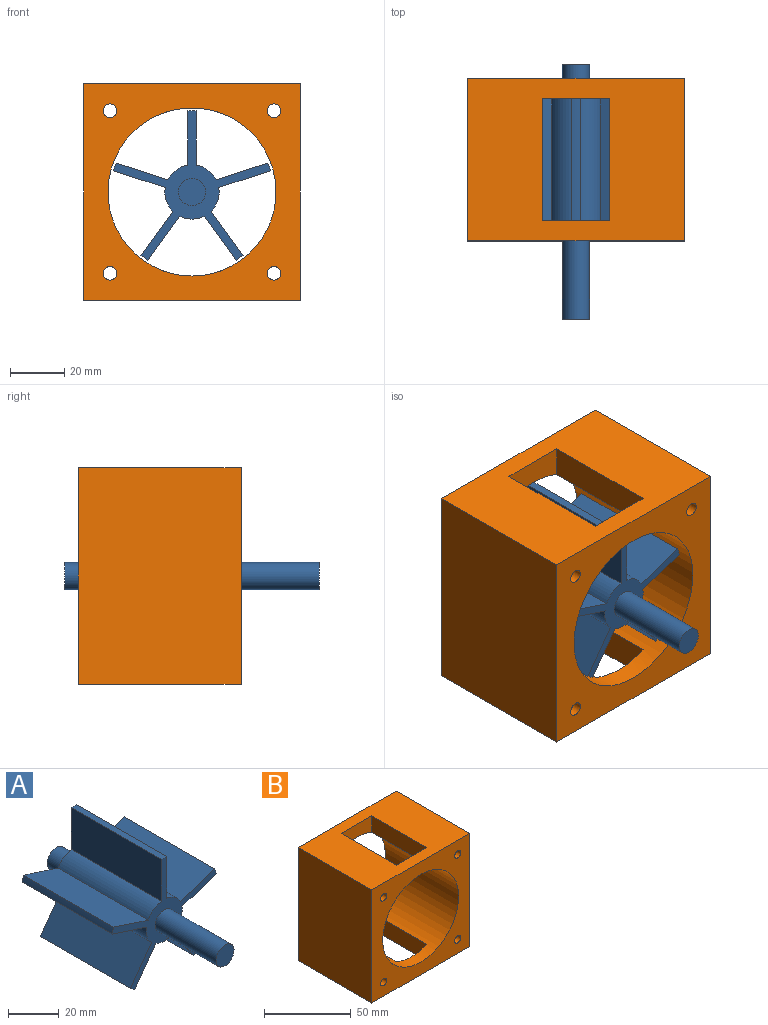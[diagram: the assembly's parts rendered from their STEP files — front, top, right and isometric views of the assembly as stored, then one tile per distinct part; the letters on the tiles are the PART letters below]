
ASSEMBLY  parts=2 mates=1
PART A: 26 faces, bbox 57.9x93.8x55.1 mm
  f0: plane 50x20.08mm, normal (1,0,0), area 1003.8mm2, adj f1,f19,f20,f21
  f1: cylinder r=30mm len=50mm, axis (0,1,0), area 150.1mm2, adj f0,f2,f20,f21
  f2: plane 50x20.08mm, normal (-1,0,0), area 1003.8mm2, adj f1,f3,f20,f21
  f3: cylinder r=10mm len=50mm, axis (0,1,0), area 477.8mm2, adj f2,f4,f20,f21
  f4: plane 50x19.09mm, normal (0.31,0,0.95), area 1003.8mm2, adj f3,f5,f20,f21
  f5: cylinder r=30mm len=50mm, axis (0,1,0), area 150.1mm2, adj f4,f6,f20,f21
  f6: plane 50x19.09mm, normal (-0.31,0,-0.95), area 1003.8mm2, adj f5,f7,f20,f21
  f7: cylinder r=10mm len=50mm, axis (0,1,0), area 477.8mm2, adj f6,f8,f20,f21
  f8: plane 50x16.24mm, normal (-0.81,0,0.59), area 1003.8mm2, adj f7,f9,f20,f21
  f9: cylinder r=30mm len=50mm, axis (0,1,0), area 150.1mm2, adj f8,f10,f20,f21
  f10: plane 50x16.24mm, normal (0.81,0,-0.59), area 1003.8mm2, adj f9,f11,f20,f21
  f11: cylinder r=10mm len=50mm, axis (0,1,0), area 477.8mm2, adj f10,f12,f20,f21
  f12: plane 50x16.24mm, normal (-0.81,0,-0.59), area 1003.8mm2, adj f11,f13,f20,f21
  f13: cylinder r=30mm len=50mm, axis (0,1,0), area 150.1mm2, adj f12,f14,f20,f21
  f14: plane 50x16.24mm, normal (0.81,0,0.59), area 1003.8mm2, adj f13,f15,f20,f21
  f15: cylinder r=10mm len=50mm, axis (0,1,0), area 477.8mm2, adj f14,f16,f20,f21
  f16: plane 50x19.09mm, normal (0.31,0,-0.95), area 1003.8mm2, adj f15,f17,f20,f21
  f17: cylinder r=30mm len=50mm, axis (0,1,0), area 150.1mm2, adj f16,f18,f20,f21
  f18: plane 50x19.09mm, normal (-0.31,0,0.95), area 1003.8mm2, adj f17,f19,f20,f21
  f19: cylinder r=10mm len=50mm, axis (0,1,0), area 477.8mm2, adj f0,f18,f20,f21
  f20: plane 57.92x55.12mm, normal (0,-1,0), area 536mm2, adj f0,f1,f2,f3,f4,f5,f6,f7
  f21: plane 57.92x55.12mm, normal (0,1,0), area 536mm2, adj f0,f1,f2,f3,f4,f5,f6,f7
  f22: cylinder r=5mm len=33.8mm, axis (0,1,0), area 1061.9mm2, adj f20,f23
  f23: plane 10x10mm, normal (0,-1,0), area 78.5mm2, adj f22
  f24: cylinder r=5mm len=10mm, axis (0,-1,0), area 314.2mm2, adj f21,f25
  f25: plane 10x10mm, normal (0,1,0), area 78.5mm2, adj f24
PART B: 19 faces, bbox 80x60x80 mm
  f0: plane 80x80mm, normal (0,-1,0), area 3302.4mm2, adj f2,f3,f4,f5,f6,f15,f16,f17
  f1: plane 80x80mm, normal (0,1,0), area 3302.4mm2, adj f2,f3,f4,f5,f6,f15,f16,f17
  f2: plane 80x60mm, normal (0,0,1), area 3675mm2, adj f0,f1,f5,f6,f11,f12,f13,f14
  f3: plane 80x60mm, normal (0,0,-1), area 3675mm2, adj f0,f1,f5,f6,f7,f8,f9,f10
  f4: cylinder r=31mm len=62mm, axis (0,1,0), area 9370.8mm2, adj f0,f1,f7,f8,f9,f10,f11,f12
  f5: plane 80x60mm, normal (-1,0,0), area 4800mm2, adj f0,f1,f2,f3
  f6: plane 80x60mm, normal (1,0,0), area 4800mm2, adj f0,f1,f2,f3
  f7: plane 45x11.63mm, normal (-1,0,0), area 523.4mm2, adj f3,f4,f8,f10
  f8: plane 25x11.63mm, normal (0,1,0), area 246.5mm2, adj f3,f4,f7,f9
  f9: plane 45x11.63mm, normal (1,0,0), area 523.4mm2, adj f3,f4,f8,f10
  f10: plane 25x11.63mm, normal (0,-1,0), area 246.5mm2, adj f3,f4,f7,f9
  f11: plane 25x11.63mm, normal (0,-1,0), area 246.5mm2, adj f2,f4,f12,f14
  f12: plane 45x11.63mm, normal (1,0,0), area 523.4mm2, adj f2,f4,f11,f13
  f13: plane 25x11.63mm, normal (0,1,0), area 246.5mm2, adj f2,f4,f12,f14
  f14: plane 45x11.63mm, normal (-1,0,0), area 523.4mm2, adj f2,f4,f11,f13
  f15: cylinder r=2.5mm len=60mm, axis (0,1,0), area 942.5mm2, adj f0,f1
  f16: cylinder r=2.5mm len=60mm, axis (0,1,0), area 942.5mm2, adj f0,f1
  f17: cylinder r=2.5mm len=60mm, axis (0,1,0), area 942.5mm2, adj f0,f1
  f18: cylinder r=2.5mm len=60mm, axis (0,1,0), area 942.5mm2, adj f0,f1
PLACE A at identity
PLACE B at identity
MATE revolute A.f19 <-> B.f4  axis (0,1,0) through (0,0,0)mm
